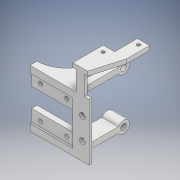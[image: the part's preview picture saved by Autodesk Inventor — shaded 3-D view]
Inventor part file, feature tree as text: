
AUTODESK INVENTOR PART (.ipt)
format: ipt  version: 2018.3 (Build 223284000, 284)  size: 1,124,864 bytes
history: native  units: mm
features: extrude x100, sketch x59, other x2, fillet x2
ambient origin geometry x8: Origin, YZ Plane, XZ Plane, XY Plane, X Axis, Y Axis, Z Axis, Center Point
bodies: Body1 (feature_tree)
feature tree (163):
  other  "Sólido1"
  extrude  "Extrusión1"  Depth=10.0mm TaperAngle=0.0deg
  extrude  "Extrusión2"  Depth=33.0mm TaperAngle=0.0deg
  extrude  "Extrusión3"  Depth=29.0mm TaperAngle=0.0deg
  extrude  "Extrusión4"  Depth=21.0mm
  extrude  "Extrusión5"  Depth=4.0mm TaperAngle=0.0deg
  extrude  "Extrusión6"  Depth=37.0mm TaperAngle=0.0deg
  extrude  "Extrusión7"  Depth=94.0mm TaperAngle=0.0deg
  extrude  "Extrusión8"  Depth=15.0mm
  extrude  "Extrusión9"  Depth=64.0mm TaperAngle=0.0deg
  extrude  "Extrusión10"  Depth=10.0mm
  extrude  "Extrusión11"  Depth=64.0mm TaperAngle=0.0deg
  extrude  "Extrusión13"  Depth=10.0mm
  extrude  "Extrusión14"  Depth=10.0mm
  extrude  "Extrusión15"  Depth=19.0mm TaperAngle=0.0deg
  extrude  "Extrusión17"  Depth=19.0mm TaperAngle=0.0deg
  extrude  "Extrusión18"  Depth=15.0mm TaperAngle=0.0deg
  extrude  "Extrusión19"  Depth=3.0mm
  extrude  "Extrusión20"  Depth=6.0mm TaperAngle=0.0deg
  extrude  "Extrusión21"  Depth=10.0mm TaperAngle=0.0deg
  extrude  "Extrusión22"  Depth=10.0mm TaperAngle=0.0deg
  extrude  "Extrusión23"  Depth=10.0mm TaperAngle=0.0deg
  extrude  "Extrusión27"  Depth=15.0mm
  extrude  "Extrusión28"  Depth=5.0mm
  extrude  "Extrusión29"  Depth=4.0mm TaperAngle=0.0deg
  extrude  "Extrusión30"  Depth=24.5mm TaperAngle=0.0deg
  extrude  "Extrusión31"  Depth=24.5mm TaperAngle=0.0deg
  extrude  "Extrusión32"  Depth=4.3mm
  extrude  "Extrusión33"  Depth=3.7mm
  extrude  "Extrusión35"  Depth=3.7mm
  extrude  "Extrusión36"  Depth=25.5mm TaperAngle=0.0deg
  extrude  "Extrusión38"  Depth=5.2mm
  extrude  "Extrusión39"  Depth=5.2mm
  extrude  "Extrusión40"  Depth=45.25mm TaperAngle=0.0deg
  extrude  "Extrusión41"  Depth=71.0mm TaperAngle=0.0deg
  extrude  "Extrusión42"  Depth=1.7mm TaperAngle=0.0deg
  extrude  "Extrusión43"  Depth=33.0mm
  extrude  "Extrusión44"  Depth=2.4mm TaperAngle=0.0deg
  extrude  "Extrusión45"  Depth=85.9mm TaperAngle=0.0deg
  extrude  "Extrusión46"  Depth=2.973mm
  extrude  "Extrusión47"  Depth=3.7mm
  extrude  "Extrusión48"  Depth=3.7mm
  extrude  "Extrusión49"  Depth=5.0mm TaperAngle=0.0deg
  extrude  "Extrusión50"  Depth=0.534mm
  extrude  "Extrusión53"  Depth=2.384mm TaperAngle=0.0deg
  extrude  "Extrusión54"  Depth=5.884mm TaperAngle=0.0deg
  extrude  "Extrusión55"  Depth=14.25mm TaperAngle=0.0deg
  extrude  "Extrusión56"  Depth=11.0mm TaperAngle=0.0deg
  extrude  "Extrusión57"  Depth=3.1mm
  sketch  "Boceto57"  dims[d115=23.0mm d116=0.0mm d117=4.0mm d118=0.0mm]
  extrude  "Extrusión58"  Depth=11.0mm
  extrude  "Extrusión59"  Depth=11.0mm TaperAngle=0.0deg
  extrude  "Extrusión60"  Depth=13.0mm TaperAngle=0.0deg
  extrude  "Extrusión61"  Depth=14.0mm TaperAngle=0.0deg
  extrude  "Extrusión62"  Depth=4.3mm
  extrude  "Extrusión63"  Depth=5.0mm TaperAngle=0.0deg
  extrude  "Extrusión64"  Depth=21.5mm TaperAngle=0.0deg
  extrude  "Extrusión65"  Depth=8.0mm TaperAngle=0.0deg
  extrude  "Extrusión66"  Depth=8.0mm TaperAngle=0.0deg
  extrude  "Extrusión67"  Depth=4.0mm TaperAngle=0.0deg
  extrude  "Extrusión68"  Depth=8.0mm TaperAngle=0.0deg
  extrude  "Extrusión69"  Depth=0.135mm
  extrude  "Extrusión74"  Depth=4.0mm TaperAngle=0.0deg
  extrude  "Extrusión75"  Depth=4.3mm TaperAngle=0.0deg
  extrude  "Extrusión76"  Depth=4.3mm TaperAngle=0.0deg
  extrude  "Extrusión77"  Depth=15.0mm TaperAngle=0.0deg
  extrude  "Extrusión78"  Depth=15.0mm TaperAngle=0.0deg
  extrude  "Extrusión79"  Depth=15.0mm TaperAngle=0.0deg
  extrude  "Extrusión80"  Depth=15.0mm TaperAngle=0.0deg
  extrude  "Extrusión81"  Depth=15.0mm TaperAngle=0.0deg
  extrude  "Extrusión82"  Depth=15.0mm TaperAngle=0.0deg
  extrude  "Extrusión83"  Depth=1.17mm TaperAngle=0.0deg
  extrude  "Extrusión84"  Depth=79.25mm TaperAngle=0.0deg
  extrude  "Extrusión85"  Depth=5.0mm TaperAngle=0.0deg
  extrude  "Extrusión86"  Depth=5.0mm TaperAngle=0.0deg
  extrude  "Extrusión87"  Depth=0.03mm TaperAngle=0.0deg
  extrude  "Extrusión88"  Depth=4.0mm TaperAngle=0.0deg
  extrude  "Extrusión89"  Depth=4.0mm TaperAngle=0.0deg
  extrude  "Extrusión90"  Depth=3.0mm
  extrude  "Extrusión91"  Depth=4.0mm TaperAngle=0.0deg
  extrude  "Extrusión92"  Depth=2.53mm TaperAngle=0.0deg
  extrude  "Extrusión93"  Depth=4.0mm TaperAngle=0.0deg
  extrude  "Extrusión94"  Depth=4.0mm TaperAngle=0.0deg
  extrude  "Extrusión95"  Depth=5.0mm TaperAngle=0.0deg
  extrude  "Extrusión96"  Depth=2.6mm TaperAngle=0.0deg
  extrude  "Extrusión97"  Depth=5.4mm
  extrude  "Extrusión98"  Depth=5.4mm
  extrude  "Extrusión99"  Depth=28.5mm TaperAngle=0.0deg
  extrude  "Extrusión100"  Depth=5.4mm
  extrude  "Extrusión101"  Depth=28.5mm TaperAngle=0.0deg
  extrude  "Extrusión102"  Depth=5.4mm
  extrude  "Extrusión103"  Depth=5.4mm
  extrude  "Extrusión109"  Depth=28.5mm TaperAngle=0.0deg
  extrude  "Extrusión110"  Depth=3.5mm TaperAngle=0.0deg
  extrude  "Extrusión112"  Depth=2.5mm
  extrude  "Extrusión113"  Depth=3.7mm
  extrude  "Extrusión114"  Depth=2.5mm
  extrude  "Extrusión115"  Depth=3.7mm
  extrude  "Extrusión116"  Depth=2.5mm
  extrude  "Extrusión117"  Depth=3.7mm
  extrude  "Extrusión118"  Depth=2.5mm
  extrude  "Extrusión121"  Depth=3.7mm
  fillet  "Empalme5"  Radius=9.75mm
  fillet  "Empalme6"  Radius=5.0mm
  sketch  "Boceto1"  dims[d0=18.0mm d1=0.0mm d2=10.0mm d3=0.0mm]
  sketch  "Boceto2"  dims[d6=3.0mm d7=33.0mm d8=0.0mm]
  sketch  "Boceto4"  dims[d9=35.0mm d10=29.0mm d11=0.0mm]
  sketch  "Boceto5"  dims[d12=2.0mm d13=21.0mm]
  sketch  "Boceto6"  dims[d14=20.0mm d15=4.0mm d16=0.0mm]
  sketch  "Boceto7"  dims[d17=8.0mm d18=0.0mm d19=37.0mm d20=0.0mm]
  sketch  "Boceto8"  dims[d21=2.0mm d22=94.0mm d23=0.0mm]
  sketch  "Boceto9"  dims[d30=5.0mm d31=15.0mm]
  sketch  "Boceto21"  dims[d32=15.0mm d33=64.0mm d34=0.0mm]
  sketch  "Boceto24"  dims[d35=64.0mm d36=0.0mm d38=10.0mm]
  sketch  "Boceto27"  dims[d40=15.0mm d41=64.0mm d42=0.0mm]
  sketch  "Boceto30"  dims[d48=46.25mm d49=10.0mm]
  sketch  "Boceto31"  dims[d50=23.0mm d51=0.0mm d52=10.0mm]
  sketch  "Boceto32"  dims[d53=19.0mm d54=0.0mm d58=19.0mm d59=0.0mm]
  sketch  "Boceto35"  dims[d68=19.0mm d69=0.0mm d70=19.0mm d71=0.0mm]
  sketch  "Boceto39"  dims[d73=19.0mm d74=0.0mm d76=15.0mm d77=0.0mm]
  sketch  "Boceto40"  dims[d78=4.0mm d79=0.0mm d80=3.0mm]
  sketch  "Boceto43"  dims[d81=6.0mm d82=0.0mm d87=6.0mm d88=0.0mm]
  sketch  "Boceto45"  dims[d89=4.0mm d96=10.0mm d97=0.0mm]
  sketch  "Boceto49"  dims[d101=10.0mm d102=0.0mm d104=10.0mm d105=0.0mm]
  sketch  "Boceto54"  dims[d106=2.0mm d107=10.0mm d108=0.0mm]
  sketch  "Boceto55"  dims[d110=11.0mm d111=15.0mm]
  sketch  "Boceto56"  dims[d112=10.0mm d113=0.0mm d114=5.0mm]
  sketch  "Boceto59"  dims[d124=24.5mm d125=0.0mm d132=24.5mm d133=0.0mm]
  sketch  "Boceto62"  dims[d141=24.5mm d142=0.0mm d145=24.5mm d146=0.0mm]
  sketch  "Boceto63"  dims[d147=10.0mm d148=0.0mm d149=4.3mm]
  sketch  "Boceto64"  dims[d150=4.3mm d151=3.7mm]
  sketch  "Boceto65"  dims[d152=3.7mm d153=3.7mm]
  sketch  "Boceto66"  dims[d154=3.7mm d155=25.5mm d156=0.0mm]
  sketch  "Boceto70"  dims[d157=5.2mm d158=5.2mm]
  sketch  "Boceto75"  dims[d159=25.5mm d160=0.0mm d161=5.2mm]
  sketch  "Boceto76"  dims[d162=5.2mm d163=45.25mm d164=0.0mm]
  sketch  "Boceto83"  dims[d165=2.6mm d166=71.0mm d167=0.0mm]
  sketch  "Boceto84"  dims[d168=10.005mm d169=1.7mm d170=0.0mm]
  sketch  "Boceto90"  dims[d171=33.0mm d172=33.0mm]
  sketch  "Boceto92"  dims[d173=38.28mm d174=4.0mm d175=0.0mm d176=0.0mm d178=2.4mm d179=0.0mm]
  sketch  "Boceto93"  dims[d180=6.15mm d181=0.0mm d184=85.9mm d185=0.0mm]
  sketch  "Boceto94"  dims[d186=2.973mm d187=2.973mm]
  sketch  "Boceto96"  dims[d188=5.0mm d189=0.0mm d205=3.7mm]
  sketch  "Boceto97"  dims[d209=3.7mm d210=3.7mm]
  sketch  "Boceto99"  dims[d211=3.7mm d212=5.0mm d213=0.0mm]
  sketch  "Boceto100"  dims[d214=5.0mm d215=0.0mm d216=0.534mm]
  sketch  "Boceto101"  dims[d217=5.0mm d218=0.0mm d219=2.384mm d220=0.0mm]
  sketch  "Boceto102"  dims[d221=17.6mm d222=5.884mm d223=0.0mm]
  sketch  "Boceto103"  dims[d224=3.25mm d225=14.25mm d226=0.0mm]
  sketch  "Boceto104"  dims[d227=11.0mm d228=0.0mm d229=11.0mm d230=0.0mm]
  sketch  "Boceto105"  dims[d233=3.1mm d234=3.1mm]
  sketch  "Boceto106"  dims[d235=11.0mm d236=0.0mm d237=11.0mm]
  sketch  "Boceto114"  dims[d238=11.0mm d239=11.0mm d240=0.0mm]
  sketch  "Boceto115"  dims[d241=11.0mm d242=0.0mm d243=13.0mm d244=0.0mm]
  sketch  "Boceto116"  dims[d245=23.0mm d246=0.0mm d247=14.0mm d248=0.0mm]
  sketch  "Boceto117"  dims[d249=15.0mm d250=0.0mm d251=4.3mm]
  sketch  "Boceto118"  dims[d252=8.0mm d253=0.0mm d254=5.0mm d255=0.0mm]
  sketch  "Boceto119"  dims[d268=1.0mm d269=21.5mm d270=0.0mm]
  sketch  "Boceto121"  dims[d271=0.389mm d272=8.0mm d273=0.0mm]
  sketch  "Boceto122"  dims[d276=8.0mm d277=0.0mm d279=8.0mm d280=0.0mm]
  sketch  "Boceto123"  dims[d282=8.0mm d283=0.0mm d285=4.0mm d286=0.0mm]
  sketch  "Boceto124"  dims[d288=4.0mm d289=0.0mm d291=8.0mm d292=0.0mm d293=0.135mm d294=4.0mm d295=0.0mm d296=4.3mm d297=0.0mm d299=4.3mm d300=0.0mm d303=15.0mm d304=0.0mm d306=15.0mm d307=0.0mm d309=15.0mm d310=0.0mm d311=15.0mm d312=0.0mm d314=15.0mm d315=0.0mm d316=15.0mm d317=0.0mm d318=1.17mm d319=0.0mm d320=79.25mm d321=0.0mm d334=5.0mm d335=0.0mm d336=5.0mm d337=0.0mm d338=0.03mm d339=0.0mm d340=4.0mm d341=0.0mm d342=4.0mm d343=0.0mm d344=3.0mm d345=4.0mm d346=0.0mm d347=2.53mm d348=0.0mm d349=4.0mm d350=0.0mm d352=4.0mm d353=0.0mm d354=5.0mm d355=0.0mm d356=2.6mm d357=0.0mm d381=5.4mm d382=5.4mm d383=28.5mm d384=0.0mm d385=5.4mm d386=28.5mm d387=0.0mm d388=5.4mm d389=5.4mm d392=28.5mm d393=0.0mm d394=3.5mm d395=0.0mm d396=2.5mm d397=3.7mm d398=2.5mm d399=3.7mm d400=2.5mm d401=3.7mm d402=2.5mm d403=3.7mm d404=9.75mm d405=0.0mm d406=5.0mm d407=0.0mm d412=20.0mm d413=39.3mm d414=40.0mm d415=39.3mm d416=1.5mm d417=0.0mm d418=3.5mm d419=2.6mm d420=0.0mm d421=2.4mm d422=0.0mm d427=1.5mm d428=0.0mm d429=27.5mm d430=27.5mm]
  other  "Saliente-Extruir7"
